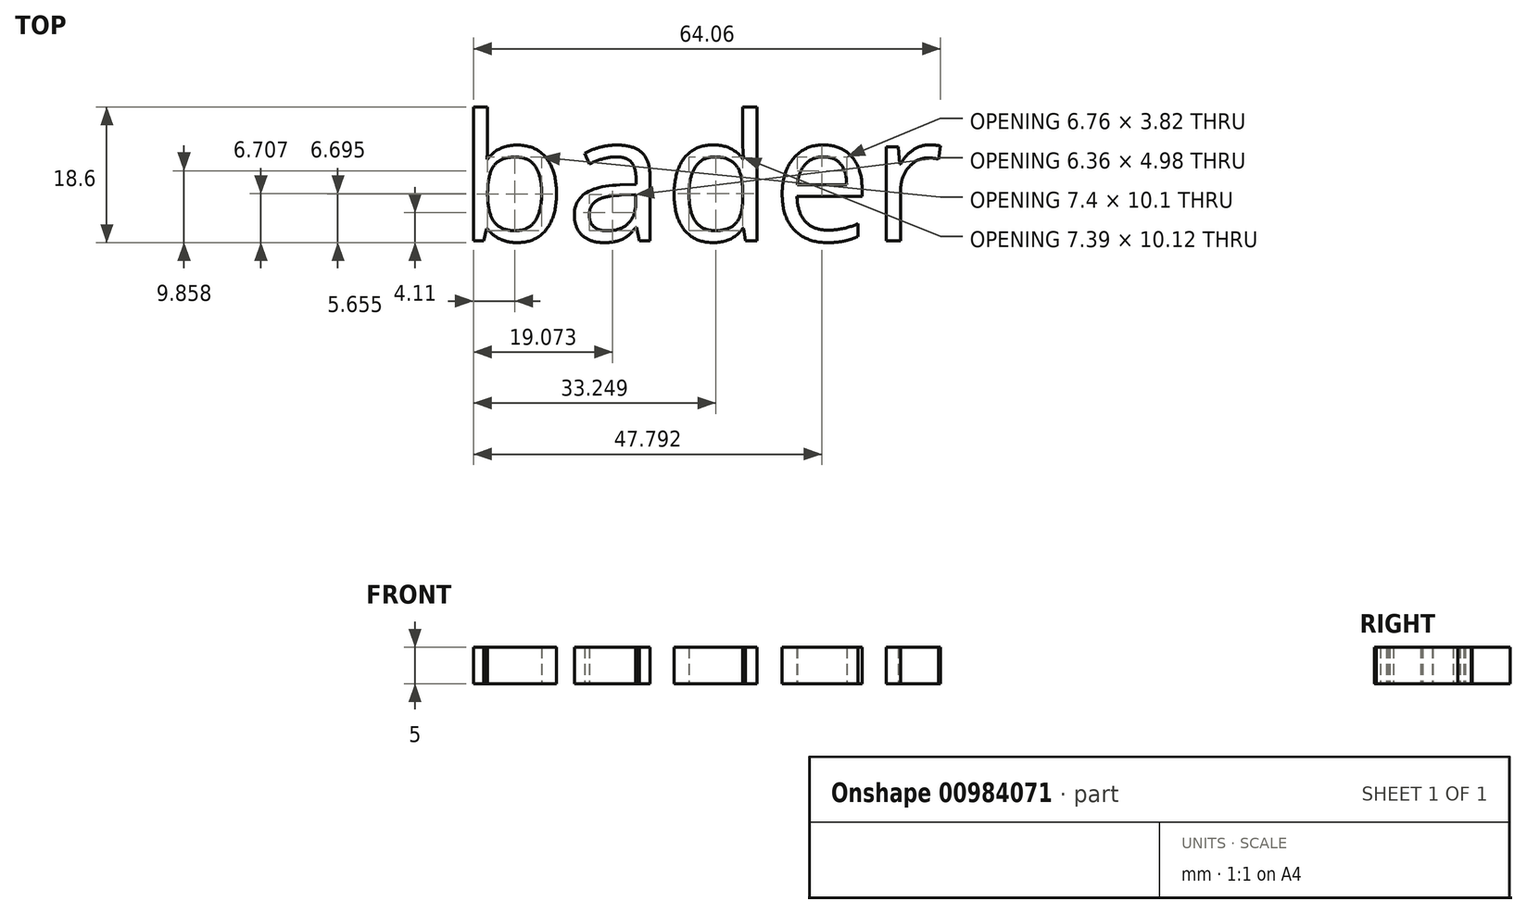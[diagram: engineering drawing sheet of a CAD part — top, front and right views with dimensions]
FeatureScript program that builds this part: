
annotation { "Feature Type Name" : "Feature", "Feature Type Description" : "" }
export const myFeature = defineFeature(function(context is Context, id is Id, definition is map)
    precondition{}
    {
        {
            var Q0;
            Q0=qCreatedBy(makeId("Top.planeOp"),FACE);
            var sketch = newSketch(context, id + "F0", { "sketchPlane" : qUnion([Q0])});
            skText(sketch, "E0", { "text": "bader", "fontName": "OpenSans-Regular.ttf"});
            const initialGuessF0  = {"E0": [0, 0, 1, 0, 0.0174]};
            skSetInitialGuess(sketch, initialGuessF0);
            skSolve(sketch);
        }
        {
            var Q0;
            Q0 = qSketchRegion(id + "F0", true);
            extrude(context, id + "F1", {"entities" : qUnion([Q0]), "depth" : 5 * mm, "offsetDistance" : 25 * mm});
        }
    });
